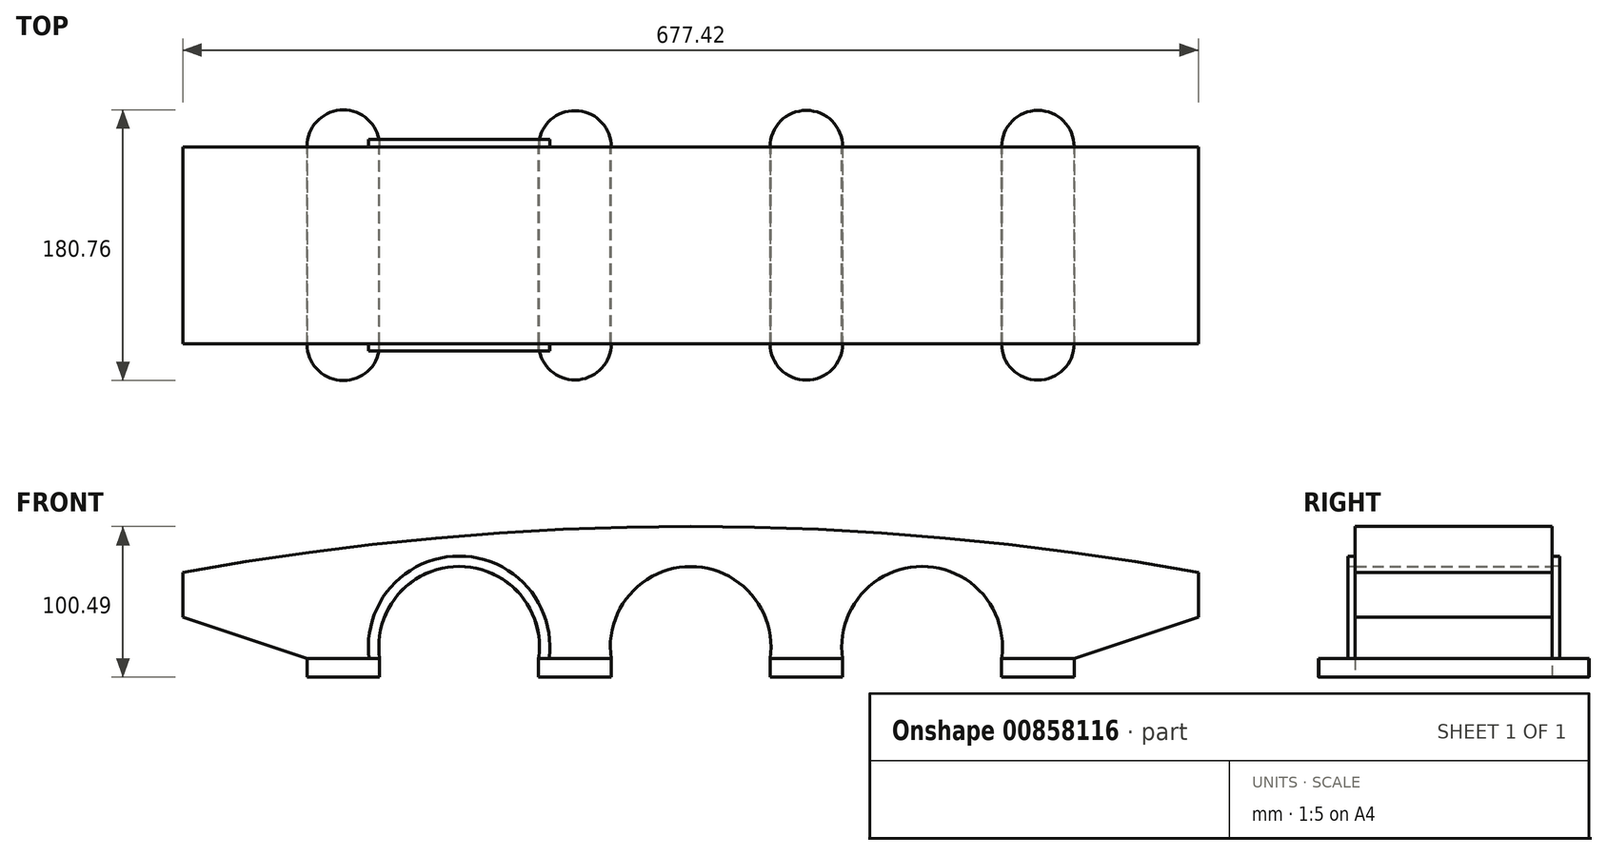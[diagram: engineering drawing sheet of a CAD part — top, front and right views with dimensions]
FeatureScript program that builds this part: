
annotation { "Feature Type Name" : "Feature", "Feature Type Description" : "" }
export const myFeature = defineFeature(function(context is Context, id is Id, definition is map)
    precondition{}
    {
        {
            var Q0;
            Q0=qCreatedBy(makeId("Front.planeOp"),FACE);
            var sketch = newSketch(context, id + "F0", { "sketchPlane" : qUnion([Q0])});
            skLineSegment(sketch, "E0", {"start": v(-237.2, -27.88) * mm, "end": v(-188.77, -27.88) * mm});
            skLineSegment(sketch, "E1", {"start": v(-237.2, -27.88) * mm, "end": v(-320.04, 0) * mm});
            skLineSegment(sketch, "E2", {"start": v(-320.04, 0) * mm, "end": v(-320.04, 29.8) * mm});
            skLineSegment(sketch, "E3", {"start": v(274.55, -27.88) * mm, "end": v(357.38, 0) * mm});
            skLineSegment(sketch, "E4", {"start": v(357.38, 0) * mm, "end": v(357.38, 29.8) * mm});
            skLineSegment(sketch, "E5", {"start": v(353.19, 59.71) * mm, "end": v(-337.43, 59.71) * mm, "construction": true});
            skArc(sketch, "E6", {"start": v(357.38, 29.8) * mm, "mid": v(18.67, 60.35) * mm, "end": v(-320.04, 29.8) * mm});
            skLineSegment(sketch, "E7", {"start": v(-237.2, -93.3) * mm, "end": v(-237.2, 77.84) * mm, "construction": true});
            skLineSegment(sketch, "E8", {"start": v(274.55, -76.63) * mm, "end": v(274.55, 80.09) * mm, "construction": true});
            skLineSegment(sketch, "E9", {"start": v(-299.18, 33.71) * mm, "end": v(306.05, 33.71) * mm, "construction": true});
            skLineSegment(sketch, "E10", {"start": v(-188.77, -48.1) * mm, "end": v(-188.77, 33.71) * mm, "construction": true});
            skLineSegment(sketch, "E11", {"start": v(-82.77, -51.1) * mm, "end": v(-82.77, 33.71) * mm, "construction": true});
            skArc(sketch, "E12", {"start": v(-82.77, -27.88) * mm, "mid": v(-135.77, 33.68) * mm, "end": v(-188.77, -27.88) * mm});
            skLineSegment(sketch, "E13", {"start": v(-34.33, -46.7) * mm, "end": v(-34.33, 33.71) * mm, "construction": true});
            skLineSegment(sketch, "E14", {"start": v(71.67, -42) * mm, "end": v(71.67, 33.71) * mm, "construction": true});
            skArc(sketch, "E15", {"start": v(71.67, -27.88) * mm, "mid": v(18.67, 33.63) * mm, "end": v(-34.33, -27.88) * mm});
            skLineSegment(sketch, "E16", {"start": v(120.11, -44.55) * mm, "end": v(120.11, 33.71) * mm, "construction": true});
            skLineSegment(sketch, "E17", {"start": v(226.11, -42.84) * mm, "end": v(226.11, 33.71) * mm, "construction": true});
            skArc(sketch, "E18", {"start": v(226.11, -27.88) * mm, "mid": v(173.11, 33.7) * mm, "end": v(120.11, -27.88) * mm});
            skLineSegment(sketch, "E19.trimOffspring", {"start": v(-82.77, -27.88) * mm, "end": v(-34.33, -27.88) * mm});
            skLineSegment(sketch, "E20.trimOffspring", {"start": v(71.67, -27.88) * mm, "end": v(120.11, -27.88) * mm});
            skLineSegment(sketch, "E21.trimOffspring", {"start": v(226.11, -27.88) * mm, "end": v(274.55, -27.88) * mm});
            skLineSegment(sketch, "E22", {"start": v(18.67, -104.82) * mm, "end": v(18.67, 107.21) * mm, "construction": true});
            skSolve(sketch);
        }
        {
            var Q0;
            Q0=makeQuery(id+"F0.imprint","IMPRINT",FACE,{"disambiguationData":[TD([[makeQuery(id+"F0.imprint","IMPRINT",EDGE,{"derivedFrom":sQuery(id+"F0.wireOp",EDGE,"E0")}),1.0]])]});
            extrude(context, id + "F1", {"entities" : qUnion([Q0]), "endBound" : BoundingType.SYMMETRIC, "depth" : 131.38 * mm, "offsetDistance" : 25 * mm});
        }
        {
            var Q0;
            Q0=makeQuery(id+"F1.opExtrude","SWEPT_FACE",FACE,{"disambiguationData":[OSD([sQuery(id+"F0.wireOp",EDGE,"E19.trimOffspring")])]});
            var sketch = newSketch(context, id + "F2", { "sketchPlane" : qUnion([Q0])});
            skLineSegment(sketch, "E23", {"start": v(-188.8, -65.69) * mm, "end": v(-188.8, 65.84) * mm});
            skLineSegment(sketch, "E24", {"start": v(-82.77, -65.69) * mm, "end": v(-82.77, 65.69) * mm});
            skLineSegment(sketch, "E25", {"start": v(-34.33, 65.69) * mm, "end": v(-34.33, -65.69) * mm});
            skLineSegment(sketch, "E26", {"start": v(-237.23, -91.14) * mm, "end": v(-237.23, 76.75) * mm, "construction": true});
            skLineSegment(sketch, "E27", {"start": v(-237.23, -65.54) * mm, "end": v(-237.23, 66.16) * mm});
            skLineSegment(sketch, "E28", {"start": v(120.11, 91.99) * mm, "end": v(120.11, -127.83) * mm, "construction": true});
            skLineSegment(sketch, "E29", {"start": v(226.11, -94.89) * mm, "end": v(226.11, 88.58) * mm, "construction": true});
            skLineSegment(sketch, "E30", {"start": v(274.55, -102.84) * mm, "end": v(274.55, 92.56) * mm, "construction": true});
            skArc(sketch, "E31", {"start": v(-188.8, 65.84) * mm, "mid": v(-212.85, 90.38) * mm, "end": v(-237.23, 66.16) * mm});
            skArc(sketch, "E32", {"start": v(-237.23, -65.54) * mm, "mid": v(-213.09, -89.76) * mm, "end": v(-188.8, -65.69) * mm});
            skArc(sketch, "E33", {"start": v(-34.33, 65.69) * mm, "mid": v(-58.55, 89.9) * mm, "end": v(-82.77, 65.69) * mm});
            skArc(sketch, "E34", {"start": v(-82.77, -65.69) * mm, "mid": v(-58.55, -89.9) * mm, "end": v(-34.33, -65.69) * mm});
            skLineSegment(sketch, "E35", {"start": v(-82.77, -65.69) * mm, "end": v(-34.33, -65.69) * mm});
            skLineSegment(sketch, "E36", {"start": v(71.67, -65.69) * mm, "end": v(71.67, 65.84) * mm});
            skLineSegment(sketch, "E37", {"start": v(120.11, -65.69) * mm, "end": v(120.11, 65.84) * mm});
            skLineSegment(sketch, "E38", {"start": v(226.11, -65.69) * mm, "end": v(226.11, 65.84) * mm});
            skLineSegment(sketch, "E39", {"start": v(250.33, 65.84) * mm, "end": v(274.55, 65.84) * mm});
            skLineSegment(sketch, "E40", {"start": v(274.55, -65.69) * mm, "end": v(274.55, 65.84) * mm});
            skArc(sketch, "E41", {"start": v(120.11, 65.84) * mm, "mid": v(95.9, 90.06) * mm, "end": v(71.67, 65.84) * mm});
            skArc(sketch, "E42", {"start": v(71.67, -65.69) * mm, "mid": v(95.9, -89.9) * mm, "end": v(120.11, -65.69) * mm});
            skArc(sketch, "E43", {"start": v(226.11, -65.69) * mm, "mid": v(250.33, -89.9) * mm, "end": v(274.55, -65.7) * mm});
            skArc(sketch, "E44", {"start": v(274.55, 65.84) * mm, "mid": v(250.33, 90.06) * mm, "end": v(226.11, 65.84) * mm});
            skSolve(sketch);
        }
        {
            var Q0;
            Q0=makeQuery(id+"F2.imprint","IMPRINT",FACE,{"disambiguationData":[TD([[makeQuery(id+"F2.imprint","IMPRINT",EDGE,{"derivedFrom":sQuery(id+"F2.wireOp",EDGE,"E23")}),1.0]])]});
            var Q1;
            Q1=makeQuery(id+"F2.imprint","IMPRINT",FACE,{"disambiguationData":[TD([[makeQuery(id+"F2.imprint","IMPRINT",EDGE,{"derivedFrom":sQuery(id+"F2.wireOp",EDGE,"E24")}),1.0]])]});
            var Q2;
            Q2=makeQuery(id+"F2.imprint","IMPRINT",FACE,{"disambiguationData":[TD([[makeQuery(id+"F2.imprint","IMPRINT",EDGE,{"derivedFrom":sQuery(id+"F2.wireOp",EDGE,"E36")}),-1.0]])]});
            var Q3;
            Q3=makeQuery(id+"F2.imprint","IMPRINT",FACE,{"disambiguationData":[TD([[makeQuery(id+"F2.imprint","IMPRINT",EDGE,{"derivedFrom":sQuery(id+"F2.wireOp",EDGE,"E38")}),-1.0]])]});
            var Q4;
            Q4=makeQuery(id+"F2.imprint","IMPRINT",FACE,{"disambiguationData":[TD([[makeQuery(id+"F2.imprint","IMPRINT",EDGE,{"derivedFrom":sQuery(id+"F2.wireOp",EDGE,"E34")}),1.0]])]});
            var Q5;
            {var subQ0=sQuery(id+"F2.wireOp",EDGE,"SdlTbksm-PDRq-94gp-nlns-VF8EcEboqzC3");Q5=makeQuery(id+"F2.imprint","IMPRINT",FACE,{"disambiguationData":[TD([[makeQuery(id+"F2.imprint","IMPRINT",EDGE,{"derivedFrom":subQ0}),1.0]])]});}
            var Q6;
            Q6=makeQuery(id+"F2.imprint","IMPRINT",FACE,{"disambiguationData":[TD([[makeQuery(id+"F2.imprint","IMPRINT",EDGE,{"derivedFrom":sQuery(id+"F2.wireOp",EDGE,"E33")}),1.0]])]});
            extrude(context, id + "F3", {"entities" : qUnion([Q0, Q1, Q2, Q3, Q4, Q5, Q6]), "operationType" : NewBodyOperationType.ADD, "depth" : 12.26 * mm, "offsetDistance" : 25 * mm});
        }
        {
            var Q0;
            Q0=makeQuery(id+"F1.opExtrude","CAP_FACE",FACE,{"disambiguationData":[OSD([sQuery(id+"F0.wireOp",EDGE,"E0"),sQuery(id+"F0.wireOp",EDGE,"E1"),sQuery(id+"F0.wireOp",EDGE,"E2"),sQuery(id+"F0.wireOp",EDGE,"E3"),sQuery(id+"F0.wireOp",EDGE,"E4"),sQuery(id+"F0.wireOp",EDGE,"E6"),sQuery(id+"F0.wireOp",EDGE,"E12"),sQuery(id+"F0.wireOp",EDGE,"E15"),sQuery(id+"F0.wireOp",EDGE,"E18"),sQuery(id+"F0.wireOp",EDGE,"E19.trimOffspring"),sQuery(id+"F0.wireOp",EDGE,"E20.trimOffspring"),sQuery(id+"F0.wireOp",EDGE,"E21.trimOffspring")])],"isStart":false});
            var sketch = newSketch(context, id + "F4", { "sketchPlane" : qUnion([Q0])});
            skArc(sketch, "E45", {"start": v(-82.77, -27.88) * mm, "mid": v(-135.77, 33.68) * mm, "end": v(-188.77, -27.88) * mm});
            skLineSegment(sketch, "E46", {"start": v(-82.77, -27.88) * mm, "end": v(-82.77, -27.88) * mm});
            skLineSegment(sketch, "E47", {"start": v(-188.77, -27.88) * mm, "end": v(-188.77, -27.88) * mm});
            skArc(sketch, "E48", {"start": v(-82.77, -27.88) * mm, "mid": v(-135.77, 33.51) * mm, "end": v(-188.77, -27.88) * mm});
            skLineSegment(sketch, "E49", {"start": v(-195.78, -46.86) * mm, "end": v(-195.78, 30.82) * mm, "construction": true});
            skLineSegment(sketch, "E50", {"start": v(-75.76, -39.77) * mm, "end": v(-75.76, 13.93) * mm, "construction": true});
            skArc(sketch, "E51", {"start": v(-75.76, -27.88) * mm, "mid": v(-135.77, 40.69) * mm, "end": v(-195.78, -27.88) * mm});
            skLineSegment(sketch, "E52", {"start": v(-82.77, -27.88) * mm, "end": v(-75.76, -27.88) * mm});
            skLineSegment(sketch, "E53", {"start": v(-188.77, -27.88) * mm, "end": v(-195.78, -27.88) * mm});
            skLineSegment(sketch, "E54", {"start": v(18.67, 46.3) * mm, "end": v(18.67, -38.44) * mm, "construction": true});
            skPoint(sketch, "E54.startSnap0", {"position": v(18.67, 33.63) * mm});
            skLineSegment(sketch, "E55", {"start": v(-41.34, -47.55) * mm, "end": v(-41.34, 22.53) * mm, "construction": true});
            skLineSegment(sketch, "E56", {"start": v(78.68, -56.19) * mm, "end": v(78.68, 14.1) * mm, "construction": true});
            skArc(sketch, "E57", {"start": v(71.67, -27.88) * mm, "mid": v(18.67, 33.63) * mm, "end": v(-34.33, -27.88) * mm});
            skArc(sketch, "E58", {"start": v(78.68, -27.88) * mm, "mid": v(18.67, 40.64) * mm, "end": v(-41.34, -27.88) * mm});
            skLineSegment(sketch, "E59", {"start": v(-41.34, -27.88) * mm, "end": v(-34.33, -27.88) * mm});
            skLineSegment(sketch, "E60", {"start": v(71.67, -27.88) * mm, "end": v(78.68, -27.88) * mm});
            skLineSegment(sketch, "E61", {"start": v(173.11, 45.15) * mm, "end": v(173.11, -38.4) * mm, "construction": true});
            skPoint(sketch, "E61.startSnap0", {"position": v(173.11, 33.7) * mm});
            skLineSegment(sketch, "E62", {"start": v(113.1, -50.04) * mm, "end": v(113.1, 18.24) * mm, "construction": true});
            skArc(sketch, "E63", {"start": v(226.11, -27.88) * mm, "mid": v(173.11, 33.7) * mm, "end": v(120.11, -27.88) * mm});
            skArc(sketch, "E64", {"start": v(233.12, -27.88) * mm, "mid": v(173.11, 40.7) * mm, "end": v(113.1, -27.88) * mm});
            skLineSegment(sketch, "E65", {"start": v(113.1, -27.88) * mm, "end": v(120.11, -27.88) * mm});
            skLineSegment(sketch, "E66", {"start": v(226.11, -27.88) * mm, "end": v(233.12, -27.88) * mm});
            skArc(sketch, "E67", {"start": v(233.12, -27.88) * mm, "mid": v(173.11, 40.54) * mm, "end": v(113.1, -27.88) * mm});
            skLineSegment(sketch, "E68", {"start": v(233.12, -27.88) * mm, "end": v(226.11, -27.88) * mm});
            skLineSegment(sketch, "E69", {"start": v(120.11, -27.88) * mm, "end": v(113.1, -27.88) * mm});
            skArc(sketch, "E70", {"start": v(78.68, -27.88) * mm, "mid": v(18.67, 40.55) * mm, "end": v(-41.34, -27.88) * mm});
            skLineSegment(sketch, "E71", {"start": v(78.68, -27.88) * mm, "end": v(71.67, -27.88) * mm});
            skLineSegment(sketch, "E72", {"start": v(-34.33, -27.88) * mm, "end": v(-41.34, -27.88) * mm});
            skArc(sketch, "E73", {"start": v(-82.77, -27.88) * mm, "mid": v(-135.77, 33.8) * mm, "end": v(-188.77, -27.88) * mm});
            skArc(sketch, "E74", {"start": v(-75.76, -27.88) * mm, "mid": v(-135.77, 40.62) * mm, "end": v(-195.78, -27.88) * mm});
            skLineSegment(sketch, "E75", {"start": v(-75.76, -27.88) * mm, "end": v(-82.77, -27.88) * mm});
            skLineSegment(sketch, "E76", {"start": v(18.67, 46.3) * mm, "end": v(18.67, 160.63) * mm, "construction": true});
            skSolve(sketch);
        }
        {
            var Q0;
            Q0=makeQuery(id+"F4.imprint","IMPRINT",FACE,{"disambiguationData":[TD([[makeQuery(id+"F4.imprint","IMPRINT",EDGE,{"derivedFrom":sQuery(id+"F4.wireOp",EDGE,"E57")}),-1.0]])]});
            var Q1;
            Q1=makeQuery(id+"F4.imprint","IMPRINT",FACE,{"disambiguationData":[TD([[makeQuery(id+"F4.imprint","IMPRINT",EDGE,{"derivedFrom":sQuery(id+"F4.wireOp",EDGE,"E63")}),-1.0]])]});
            var Q2;
            {var subQ4=sQuery(id+"F4.wireOp",EDGE,"E73");Q2=makeQuery(id+"F4.imprint","IMPRINT",FACE,{"disambiguationData":[TD([[makeQuery(id+"F4.imprint","IMPRINT",EDGE,{"derivedFrom":subQ4}),-1.0]])]});}
            extrude(context, id + "F5", {"entities" : qUnion([Q0, Q1, Q2]), "operationType" : NewBodyOperationType.ADD, "depth" : 5 * mm, "offsetDistance" : 25 * mm});
        }
        {
            var Q0;
            Q0=makeQuery(id+"F1.opExtrude","SWEPT_BODY",BODY,{"disambiguationData":[OSD([sQuery(id+"F0.wireOp",EDGE,"E0"),sQuery(id+"F0.wireOp",EDGE,"E1"),sQuery(id+"F0.wireOp",EDGE,"E2"),sQuery(id+"F0.wireOp",EDGE,"E3"),sQuery(id+"F0.wireOp",EDGE,"E4"),sQuery(id+"F0.wireOp",EDGE,"E6"),sQuery(id+"F0.wireOp",EDGE,"E12"),sQuery(id+"F0.wireOp",EDGE,"E15"),sQuery(id+"F0.wireOp",EDGE,"E18"),sQuery(id+"F0.wireOp",EDGE,"E19.trimOffspring"),sQuery(id+"F0.wireOp",EDGE,"E20.trimOffspring"),sQuery(id+"F0.wireOp",EDGE,"E21.trimOffspring")])]});
            var Q1;
            Q1=qCreatedBy(makeId("Front.planeOp"),FACE);
            mirror(context, id + "F6", {"operationType" : NewBodyOperationType.ADD, "entities" : qUnion([Q0]), "mirrorPlane" : qUnion([Q1])});
        }
    });
